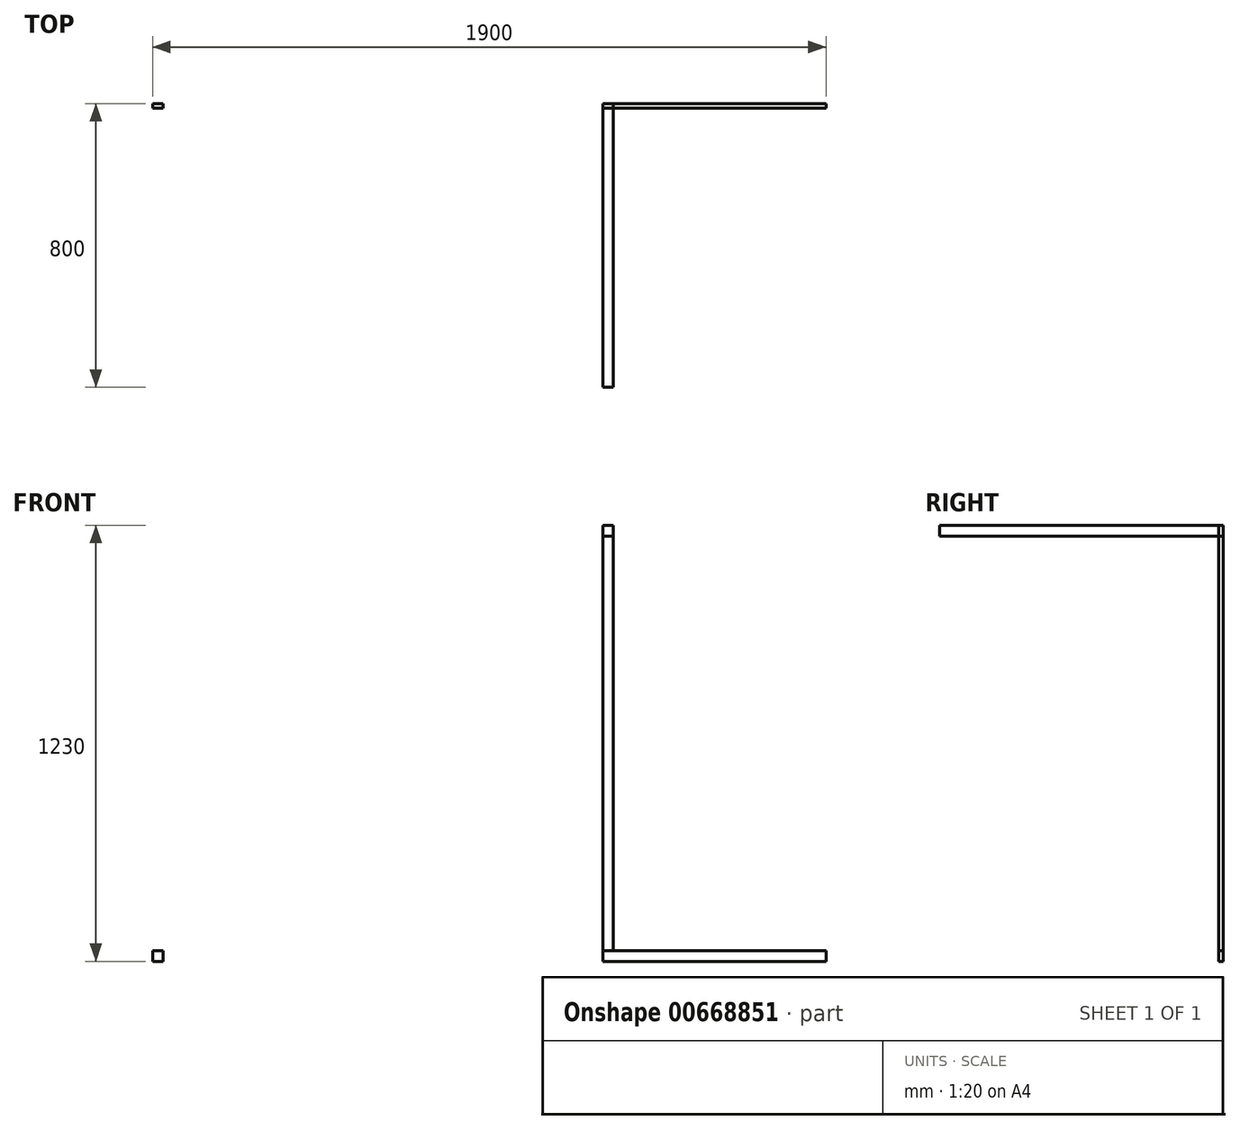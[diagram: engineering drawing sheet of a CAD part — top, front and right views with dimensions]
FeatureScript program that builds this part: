
annotation { "Feature Type Name" : "Feature", "Feature Type Description" : "" }
export const myFeature = defineFeature(function(context is Context, id is Id, definition is map)
    precondition{}
    {
        {
            var Q0;
            Q0=qCreatedBy(makeId("Front.planeOp"),FACE);
            var sketch = newSketch(context, id + "F0", { "sketchPlane" : qUnion([Q0])});
            skLineSegment(sketch, "E0.bottom", {"start": v(-950, -950) * mm, "end": v(950, -950) * mm});
            skLineSegment(sketch, "E0.top", {"start": v(-950, 950) * mm, "end": v(950, 950) * mm});
            skLineSegment(sketch, "E0.left", {"start": v(-950, -950) * mm, "end": v(-950, 950) * mm});
            skLineSegment(sketch, "E0.right", {"start": v(950, -950) * mm, "end": v(950, 950) * mm});
            skPoint(sketch, "E0.middle", {"position": v(0, 0) * mm});
            skLineSegment(sketch, "E1.bottom", {"start": v(950, -950) * mm, "end": v(350, -950) * mm});
            skLineSegment(sketch, "E1.top", {"start": v(950, 250) * mm, "end": v(350, 250) * mm});
            skLineSegment(sketch, "E1.left", {"start": v(950, -950) * mm, "end": v(950, 250) * mm});
            skLineSegment(sketch, "E1.right", {"start": v(350, -950) * mm, "end": v(350, 250) * mm});
            skLineSegment(sketch, "E2.bottom", {"start": v(-950, 950) * mm, "end": v(-920, 950) * mm});
            skLineSegment(sketch, "E2.top", {"start": v(-950, 920) * mm, "end": v(-920, 920) * mm});
            skLineSegment(sketch, "E2.left", {"start": v(-950, 950) * mm, "end": v(-950, 920) * mm});
            skLineSegment(sketch, "E2.right", {"start": v(-920, 950) * mm, "end": v(-920, 920) * mm});
            skLineSegment(sketch, "E3.bottom", {"start": v(-950, -950) * mm, "end": v(-920, -950) * mm});
            skLineSegment(sketch, "E3.top", {"start": v(-950, -920) * mm, "end": v(-920, -920) * mm});
            skLineSegment(sketch, "E3.left", {"start": v(-950, -950) * mm, "end": v(-950, -920) * mm});
            skLineSegment(sketch, "E3.right", {"start": v(-920, -950) * mm, "end": v(-920, -920) * mm});
            skLineSegment(sketch, "E4.bottom", {"start": v(350, 250) * mm, "end": v(320, 250) * mm});
            skLineSegment(sketch, "E4.top", {"start": v(350, 280) * mm, "end": v(320, 280) * mm});
            skLineSegment(sketch, "E4.left", {"start": v(350, 250) * mm, "end": v(350, 280) * mm});
            skLineSegment(sketch, "E4.right", {"start": v(320, 250) * mm, "end": v(320, 280) * mm});
            skLineSegment(sketch, "E5.bottom", {"start": v(350, -950) * mm, "end": v(320, -950) * mm});
            skLineSegment(sketch, "E5.top", {"start": v(350, -920) * mm, "end": v(320, -920) * mm});
            skLineSegment(sketch, "E5.left", {"start": v(350, -950) * mm, "end": v(350, -920) * mm});
            skLineSegment(sketch, "E5.right", {"start": v(320, -950) * mm, "end": v(320, -920) * mm});
            skLineSegment(sketch, "E6.bottom", {"start": v(320, -920) * mm, "end": v(950, -920) * mm});
            skLineSegment(sketch, "E6.top", {"start": v(320, 250) * mm, "end": v(950, 250) * mm});
            skLineSegment(sketch, "E6.left", {"start": v(320, -920) * mm, "end": v(320, 250) * mm});
            skLineSegment(sketch, "E6.right", {"start": v(950, -920) * mm, "end": v(950, 250) * mm});
            skLineSegment(sketch, "E7.bottom", {"start": v(950, 250) * mm, "end": v(920, 250) * mm});
            skLineSegment(sketch, "E7.top", {"start": v(950, 280) * mm, "end": v(920, 280) * mm});
            skLineSegment(sketch, "E7.left", {"start": v(950, 250) * mm, "end": v(950, 280) * mm});
            skLineSegment(sketch, "E7.right", {"start": v(920, 250) * mm, "end": v(920, 280) * mm});
            skLineSegment(sketch, "E8.bottom", {"start": v(950, 950) * mm, "end": v(920, 950) * mm});
            skLineSegment(sketch, "E8.top", {"start": v(950, 920) * mm, "end": v(920, 920) * mm});
            skLineSegment(sketch, "E8.left", {"start": v(950, 950) * mm, "end": v(950, 920) * mm});
            skLineSegment(sketch, "E8.right", {"start": v(920, 950) * mm, "end": v(920, 920) * mm});
            skSolve(sketch);
        }
        {
            var Q0;
            Q0=makeQuery(id+"F0.imprint","IMPRINT",FACE,{"disambiguationData":[TD([[makeQuery(id+"F0.imprint","IMPRINT",EDGE,{"derivedFrom":sQuery(id+"F0.wireOp",EDGE,"E2.bottom")}),-1.0]])]});
            var Q1;
            Q1=makeQuery(id+"F0.imprint","IMPRINT",FACE,{"disambiguationData":[TD([[makeQuery(id+"F0.imprint","IMPRINT",EDGE,{"derivedFrom":sQuery(id+"F0.wireOp",EDGE,"E8.bottom")}),1.0]])]});
            var Q2;
            Q2=makeQuery(id+"F0.imprint","IMPRINT",FACE,{"disambiguationData":[TD([[makeQuery(id+"F0.imprint","IMPRINT",EDGE,{"derivedFrom":sQuery(id+"F0.wireOp",EDGE,"E7.bottom")}),-1.0]])]});
            var Q3;
            Q3=makeQuery(id+"F0.imprint","IMPRINT",FACE,{"disambiguationData":[TD([[makeQuery(id+"F0.imprint","IMPRINT",EDGE,{"derivedFrom":sQuery(id+"F0.wireOp",EDGE,"E4.top")}),1.0]])]});
            var Q4;
            Q4=makeQuery(id+"F0.imprint","IMPRINT",FACE,{"disambiguationData":[TD([[makeQuery(id+"F0.imprint","IMPRINT",EDGE,{"derivedFrom":sQuery(id+"F0.wireOp",EDGE,"E5.bottom")}),-1.0]])]});
            var Q5;
            Q5=makeQuery(id+"F0.imprint","IMPRINT",FACE,{"disambiguationData":[TD([[makeQuery(id+"F0.imprint","IMPRINT",EDGE,{"derivedFrom":sQuery(id+"F0.wireOp",EDGE,"E3.bottom")}),1.0]])]});
            extrude(context, id + "F1", {"entities" : qUnion([Q0, Q1, Q2, Q3, Q4, Q5]), "depth" : 800 * mm, "offsetDistance" : 25 * mm});
        }
        {
            var Q0;
            Q0=makeQuery(id+"F0.imprint","IMPRINT",FACE,{"disambiguationData":[TD([[makeQuery(id+"F0.imprint","IMPRINT",EDGE,{"derivedFrom":sQuery(id+"F0.wireOp",EDGE,"E0.bottom")}),1.0]])]});
            extrude(context, id + "F2", {"entities" : qUnion([Q0]), "depth" : 12 * mm, "offsetDistance" : 25 * mm});
        }
        {
            var Q0;
            Q0=makeQuery(id+"F0.imprint","IMPRINT",FACE,{"disambiguationData":[TD([[makeQuery(id+"F0.imprint","IMPRINT",EDGE,{"derivedFrom":sQuery(id+"F0.wireOp",EDGE,"E0.bottom")}),1.0]])]});
            var Q1;
            {var subQ0=sQuery(id+"F0.wireOp",EDGE,"E1.right");Q1=makeQuery(id+"F0.imprint","IMPRINT",FACE,{"disambiguationData":[TD([[makeQuery(id+"F0.imprint","IMPRINT",EDGE,{"derivedFrom":subQ0}),1.0]])]});}
            var Q2;
            Q2=makeQuery(id+"F0.imprint","IMPRINT",FACE,{"disambiguationData":[TD([[makeQuery(id+"F0.imprint","IMPRINT",EDGE,{"derivedFrom":sQuery(id+"F0.wireOp",EDGE,"E5.bottom")}),-1.0]])]});
            var Q3;
            Q3=makeQuery(id+"F0.imprint","IMPRINT",FACE,{"disambiguationData":[TD([[makeQuery(id+"F0.imprint","IMPRINT",EDGE,{"derivedFrom":sQuery(id+"F0.wireOp",EDGE,"E4.top")}),1.0]])]});
            var Q4;
            Q4=makeQuery(id+"F0.imprint","IMPRINT",FACE,{"disambiguationData":[TD([[makeQuery(id+"F0.imprint","IMPRINT",EDGE,{"derivedFrom":sQuery(id+"F0.wireOp",EDGE,"E7.bottom")}),-1.0]])]});
            var Q5;
            Q5=makeQuery(id+"F0.imprint","IMPRINT",FACE,{"disambiguationData":[TD([[makeQuery(id+"F0.imprint","IMPRINT",EDGE,{"derivedFrom":sQuery(id+"F0.wireOp",EDGE,"E3.bottom")}),1.0]])]});
            var Q6;
            Q6=makeQuery(id+"F0.imprint","IMPRINT",FACE,{"disambiguationData":[TD([[makeQuery(id+"F0.imprint","IMPRINT",EDGE,{"derivedFrom":sQuery(id+"F0.wireOp",EDGE,"E8.bottom")}),1.0]])]});
            var Q7;
            Q7=makeQuery(id+"F0.imprint","IMPRINT",FACE,{"disambiguationData":[TD([[makeQuery(id+"F0.imprint","IMPRINT",EDGE,{"derivedFrom":sQuery(id+"F0.wireOp",EDGE,"E2.bottom")}),-1.0]])]});
            extrude(context, id + "F3", {"entities" : qUnion([Q0, Q1, Q2, Q3, Q4, Q5, Q6, Q7]), "depth" : 12 * mm, "offsetDistance" : 25 * mm});
        }
    });
